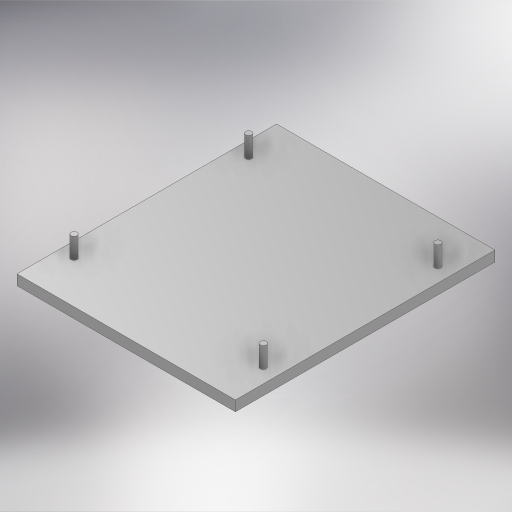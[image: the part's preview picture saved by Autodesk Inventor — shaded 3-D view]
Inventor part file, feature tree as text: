
AUTODESK INVENTOR PART (.ipt)
format: ipt  version: 2024 (Build 280153000, 153)  size: 338,432 bytes
history: native  units: mm
features: other x11, extrude x3, sketch x3
ambient origin geometry x8: Origin, YZ Plane, XZ Plane, XY Plane, X Axis, Y Axis, Z Axis, Center Point
bodies: Body1 (feature_tree)
feature tree (17):
  other  "Sólido1"
  extrude  "Extrusión1"  Depth=126.0mm
  extrude  "Extrusión2"  Depth=53.0mm
  extrude  "Extrusión3"  Depth=3.0mm
  sketch  "Boceto1"  dims[d1=106.0mm d2=126.0mm]
  sketch  "Boceto2"  dims[d3=53.0mm d4=63.0mm]
  sketch  "Boceto3"  dims[d5=5.0mm d6=0.0mm d7=3.0mm d8=20.616mm d9=7.071mm d10=10.0mm d11=0.0mm d12=52.5mm d13=126.0mm d14=106.0mm d15=52.5mm d16=35.0mm d17=35.0mm d18=35.0mm d19=35.0mm d20=35.0mm d21=2.0mm d22=0.0mm]
  other  "Finish1"
  other  "Finish2"
  other  "Finish3"
  other  "Finish4"
  other  "Finish5"
  other  "Finish6"
  other  "Finish7"
  other  "Finish8"
  other  "Finish9"
  other  "Finish10"
